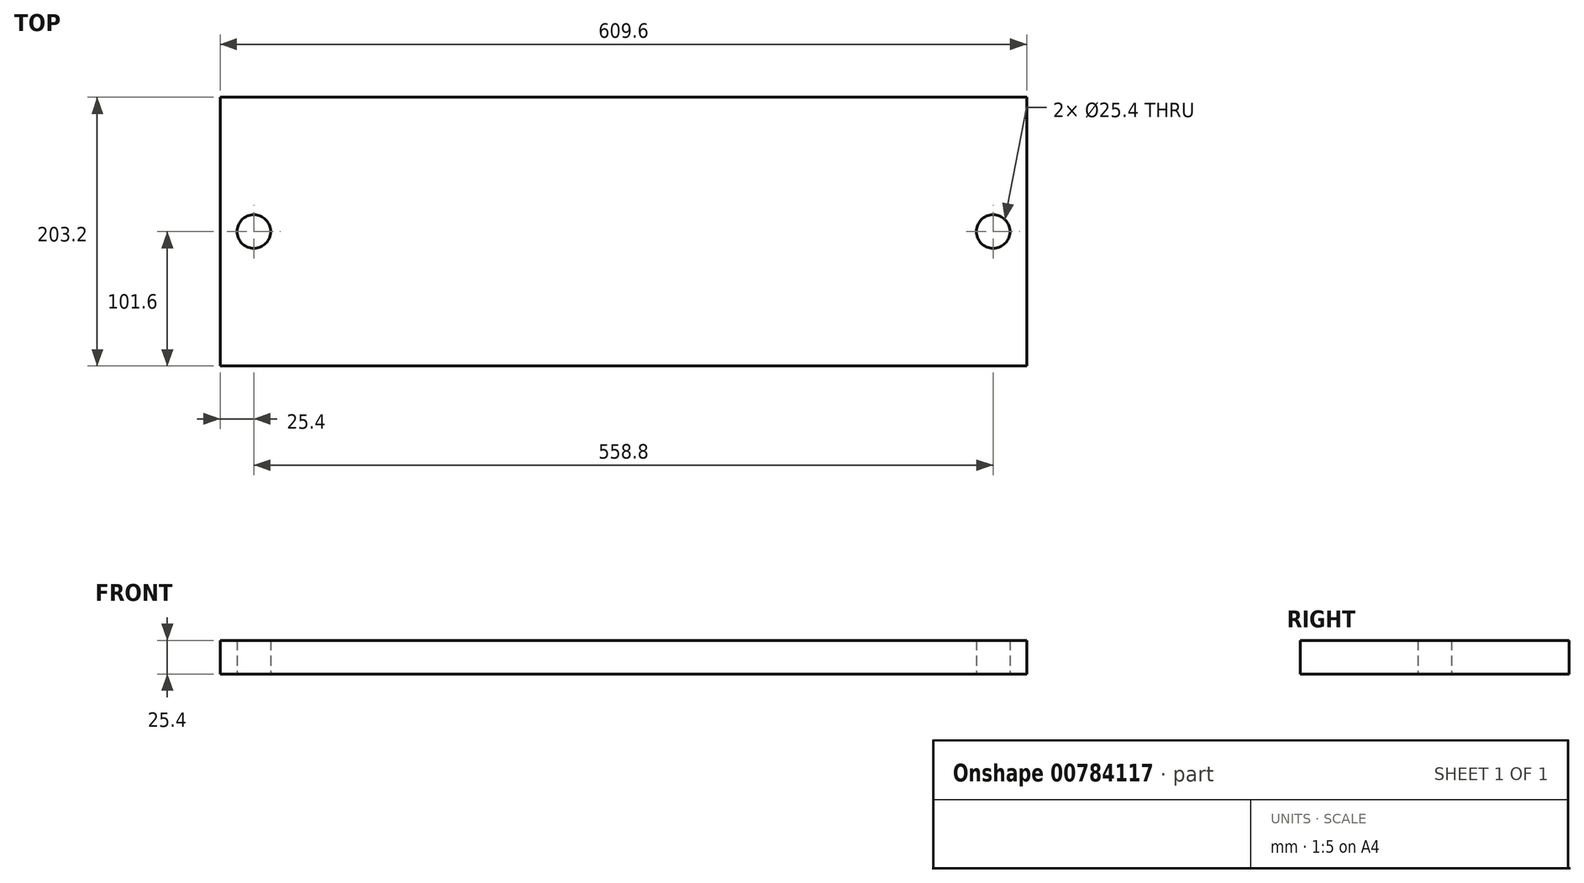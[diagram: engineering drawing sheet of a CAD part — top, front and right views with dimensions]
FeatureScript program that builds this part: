
annotation { "Feature Type Name" : "Feature", "Feature Type Description" : "" }
export const myFeature = defineFeature(function(context is Context, id is Id, definition is map)
    precondition{}
    {
        {
            var Q0;
            Q0=qCreatedBy(makeId("Top.planeOp"),FACE);
            var sketch = newSketch(context, id + "F0", { "sketchPlane" : qUnion([Q0])});
            skLineSegment(sketch, "E0.bottom", {"start": v(-304.8, 101.6) * mm, "end": v(304.8, 101.6) * mm});
            skLineSegment(sketch, "E0.top", {"start": v(-304.8, -101.6) * mm, "end": v(304.8, -101.6) * mm});
            skLineSegment(sketch, "E0.left", {"start": v(-304.8, 101.6) * mm, "end": v(-304.8, -101.6) * mm});
            skLineSegment(sketch, "E0.right", {"start": v(304.8, 101.6) * mm, "end": v(304.8, -101.6) * mm});
            skSolve(sketch);
        }
        {
            var Q0;
            Q0=makeQuery(id+"F0.imprint","IMPRINT",FACE,{"disambiguationData":[TD([[makeQuery(id+"F0.imprint","IMPRINT",EDGE,{"derivedFrom":sQuery(id+"F0.wireOp",EDGE,"E0.bottom")}),-1.0]])]});
            extrude(context, id + "F1", {"entities" : qUnion([Q0]), "depth" : 25.4 * mm, "offsetDistance" : 25.4 * mm});
        }
        {
            var Q0;
            Q0=makeQuery(id+"F1.opExtrude","CAP_FACE",FACE,{"disambiguationData":[OSD([sQuery(id+"F0.wireOp",EDGE,"E0.bottom"),sQuery(id+"F0.wireOp",EDGE,"E0.top"),sQuery(id+"F0.wireOp",EDGE,"E0.left"),sQuery(id+"F0.wireOp",EDGE,"E0.right")])],"isStart":true});
            var sketch = newSketch(context, id + "F2", { "sketchPlane" : qUnion([Q0])});
            skSolve(sketch);
        }
        {
            var Q0;
            Q0=makeQuery(id+"F2.imprint","IMPRINT",FACE,{"disambiguationData":[TD([[makeQuery(id+"F2.imprint","IMPRINT",EDGE,{"derivedFrom":makeQuery(id+"F1.opExtrude","CAP_EDGE",EDGE,{"disambiguationData":[OSD([sQuery(id+"F0.wireOp",EDGE,"E0.bottom")])],"isStart":true})}),1.0]])]});
            var sketch = newSketch(context, id + "F3", { "sketchPlane" : qUnion([Q0])});
            skCircle(sketch, "E1", {"center": v(-279.4, 0) * mm, "radius": 12.7 * mm});
            skCircle(sketch, "E2", {"center": v(279.4, 0) * mm, "radius": 12.7 * mm});
            skSolve(sketch);
        }
        {
            var Q0;
            Q0 = qSketchRegion(id + "F3", true);
            var Q1;
            Q1=makeQuery(id+"F1.opExtrude","CAP_FACE",FACE,{"disambiguationData":[OSD([sQuery(id+"F0.wireOp",EDGE,"E0.bottom"),sQuery(id+"F0.wireOp",EDGE,"E0.top"),sQuery(id+"F0.wireOp",EDGE,"E0.left"),sQuery(id+"F0.wireOp",EDGE,"E0.right")])],"isStart":false});
            extrude(context, id + "F4", {"entities" : qUnion([Q0]), "operationType" : NewBodyOperationType.REMOVE, "endBound" : BoundingType.UP_TO_SURFACE, "oppositeDirection" : true, "depth" : 25.4 * mm, "endBoundEntityFace" : qUnion([Q1]), "offsetDistance" : 25.4 * mm});
        }
    });
